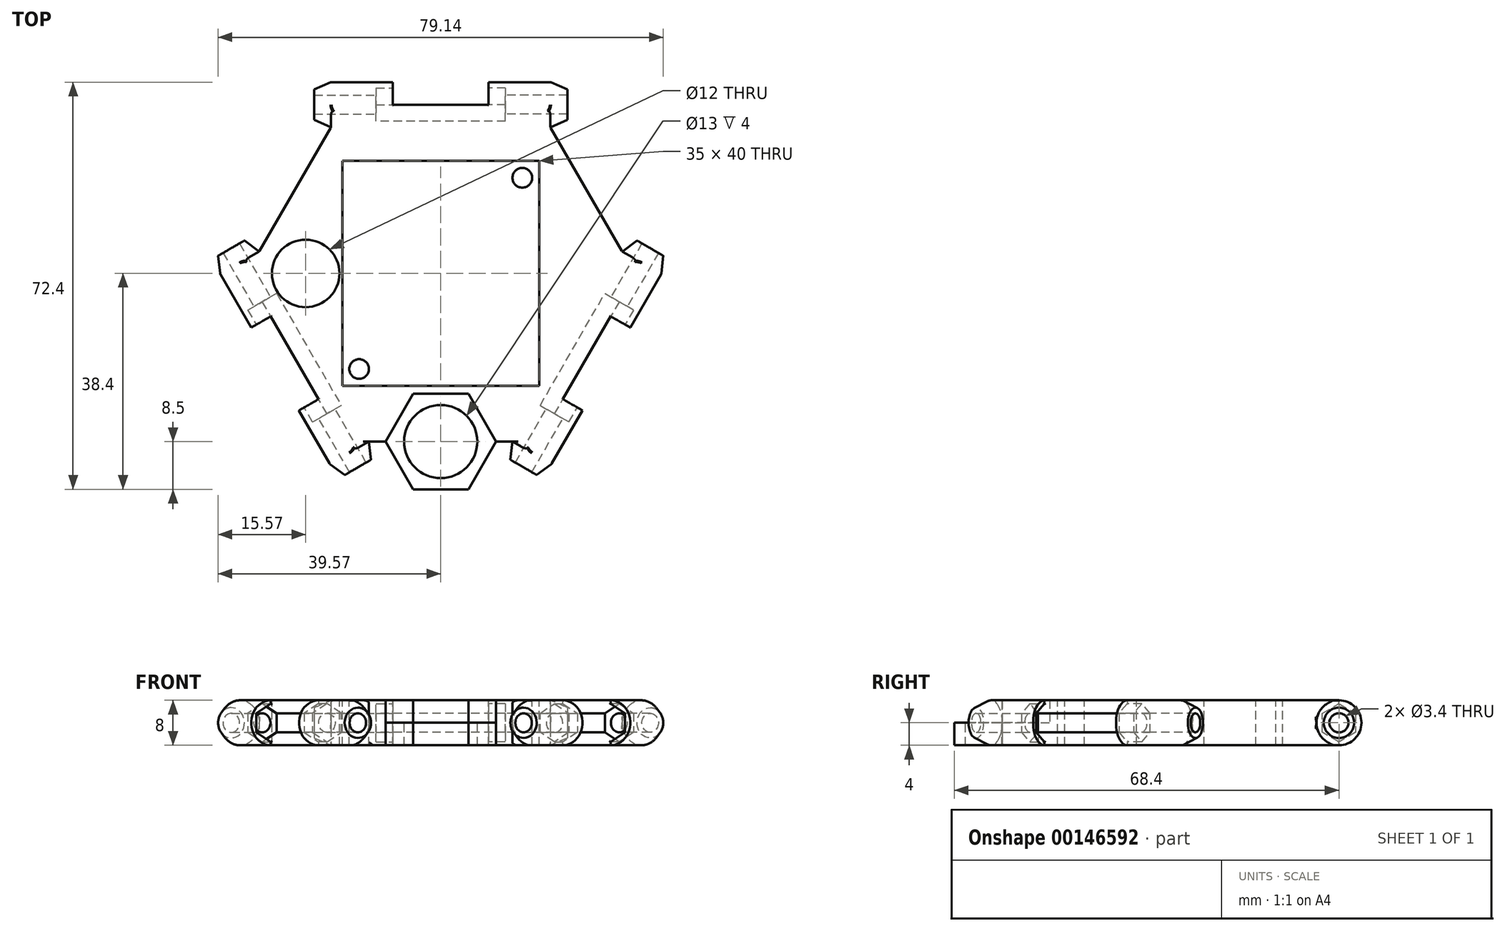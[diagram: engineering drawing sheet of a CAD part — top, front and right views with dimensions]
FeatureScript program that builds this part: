
annotation { "Feature Type Name" : "Feature", "Feature Type Description" : "" }
export const myFeature = defineFeature(function(context is Context, id is Id, definition is map)
    precondition{}
    {
        {
            var Q0;
            Q0=qCreatedBy(makeId("Top.planeOp"),FACE);
            var sketch = newSketch(context, id + "F0", { "sketchPlane" : qUnion([Q0])});
            skLineSegment(sketch, "E0.top", {"start": v(0, 34) * mm, "end": v(19.5, 34) * mm});
            skLineSegment(sketch, "E1", {"start": v(22.5, 31.7) * mm, "end": v(22.5, 32.7) * mm});
            skLineSegment(sketch, "E2", {"start": v(19.5, 34) * mm, "end": v(22.5, 32.7) * mm});
            skLineSegment(sketch, "E3", {"start": v(22.5, 31.7) * mm, "end": v(0, 31.7) * mm});
            skPoint(sketch, "E4.0.midPoint", {"position": v(0, 30) * mm});
            skLineSegment(sketch, "E5", {"start": v(19.5, 30) * mm, "end": v(36.82, 0) * mm, "construction": true});
            skLineSegment(sketch, "E6", {"start": v(0, 0) * mm, "end": v(27.62, 15.94) * mm, "construction": true});
            skLineSegment(sketch, "E7", {"start": v(0, 30) * mm, "end": v(22.5, 30) * mm, "construction": true});
            skLineSegment(sketch, "E8", {"start": v(0, 0) * mm, "end": v(0, 34) * mm});
            skLineSegment(sketch, "E9.MirrorCS", {"start": v(22.5, 28.3) * mm, "end": v(0, 28.3) * mm});
            skLineSegment(sketch, "E10.MirrorCS", {"start": v(0, 26) * mm, "end": v(19.5, 26) * mm});
            skLineSegment(sketch, "E11.MirrorCS", {"start": v(22.5, 28.3) * mm, "end": v(22.5, 27.3) * mm});
            skLineSegment(sketch, "E12.MirrorCS", {"start": v(19.5, 26) * mm, "end": v(22.5, 27.3) * mm});
            skLineSegment(sketch, "E13", {"start": v(19.5, 26) * mm, "end": v(32.2, 4) * mm, "construction": true});
            skLineSegment(sketch, "E14", {"start": v(0, 0) * mm, "end": v(25.88, 14.94) * mm});
            skLineSegment(sketch, "E15", {"start": v(19.5, 26) * mm, "end": v(25.88, 14.94) * mm});
            skSolve(sketch);
        }
        {
            var Q0;
            Q0=qCreatedBy(makeId("Right.planeOp"),FACE);
            var sketch = newSketch(context, id + "F1", { "sketchPlane" : qUnion([Q0])});
            skCircle(sketch, "E16.cCircle", {"center": v(30, 0) * mm, "radius": 2.95 * mm, "construction": true});
            skLineSegment(sketch, "E16.0", {"start": v(32.95, -1.7) * mm, "end": v(30, -3.4) * mm});
            skLineSegment(sketch, "E16.1", {"start": v(30, -3.4) * mm, "end": v(27.05, -1.7) * mm});
            skLineSegment(sketch, "E16.2", {"start": v(27.05, -1.7) * mm, "end": v(27.05, 1.7) * mm});
            skLineSegment(sketch, "E16.3", {"start": v(27.05, 1.7) * mm, "end": v(30, 3.4) * mm});
            skLineSegment(sketch, "E16.4", {"start": v(30, 3.4) * mm, "end": v(32.95, 1.7) * mm});
            skLineSegment(sketch, "E16.5", {"start": v(32.95, 1.7) * mm, "end": v(32.95, -1.7) * mm});
            skCircle(sketch, "E17", {"center": v(30, 0) * mm, "radius": 4 * mm});
            skLineSegment(sketch, "E18", {"start": v(26, 0) * mm, "end": v(26, -4) * mm});
            skLineSegment(sketch, "E19", {"start": v(26, -4) * mm, "end": v(30, -4) * mm});
            skLineSegment(sketch, "E20", {"start": v(30, 4) * mm, "end": v(30, -4) * mm, "construction": true});
            skLineSegment(sketch, "E21.MirrorCS", {"start": v(26, 4) * mm, "end": v(30, 4) * mm});
            skLineSegment(sketch, "E22.MirrorCS", {"start": v(26, 0) * mm, "end": v(26, 4) * mm});
            skLineSegment(sketch, "E23", {"start": v(0, 4) * mm, "end": v(0, -4) * mm, "construction": true});
            skLineSegment(sketch, "E24", {"start": v(30, 4) * mm, "end": v(30, 3.4) * mm});
            skLineSegment(sketch, "E25", {"start": v(30, -3.4) * mm, "end": v(30, -4) * mm});
            skSolve(sketch);
        }
        {
            var Q0;
            Q0=qCreatedBy(makeId("Top.planeOp"),FACE);
            var sketch = newSketch(context, id + "F2", { "sketchPlane" : qUnion([Q0])});
            skCircle(sketch, "E26.MirrorC", {"center": v(14.5, 17) * mm, "radius": 1.75 * mm});
            skLineSegment(sketch, "E27", {"start": v(0, 20) * mm, "end": v(17.5, 20) * mm, "construction": true});
            skLineSegment(sketch, "E28", {"start": v(17.5, 20) * mm, "end": v(17.5, 0) * mm, "construction": true});
            skLineSegment(sketch, "E29", {"start": v(17.5, 20) * mm, "end": v(0, 0) * mm, "construction": true});
            skCircle(sketch, "E30", {"center": v(10, 10) * mm, "radius": 4 * mm, "construction": true});
            skLineSegment(sketch, "E31", {"start": v(0, 10) * mm, "end": v(17.5, 10) * mm, "construction": true});
            skFitSpline(sketch, "E32", {"points": [v(12.53, 14.32) * mm, v(14.26, 12.62) * mm, v(15, 10) * mm], "startDerivative": vector(4.86, -2.41) * mm, "endDerivative": vector(0.41, -5.85) * mm});
            skLineSegment(sketch, "E33", {"start": v(15, 10) * mm, "end": v(15, 0) * mm});
            skLineSegment(sketch, "E34", {"start": v(12.53, 14.32) * mm, "end": v(2.46, 16.87) * mm});
            skLineSegment(sketch, "E35.MirrorCS", {"start": v(-12.53, 14.32) * mm, "end": v(-2.46, 16.87) * mm});
            skFitSpline(sketch, "E36.MirrorCS", {"points": [v(-12.53, 14.32) * mm, v(-14.26, 12.62) * mm, v(-15, 10) * mm], "startDerivative": vector(-4.86, -2.41) * mm, "endDerivative": vector(-0.41, -5.85) * mm});
            skLineSegment(sketch, "E37.MirrorCS", {"start": v(-15, 10) * mm, "end": v(-15, 0) * mm});
            skCircle(sketch, "E38.MirrorC", {"center": v(-14.5, 17) * mm, "radius": 1.75 * mm});
            skPoint(sketch, "E39.visualSharp", {"position": v(0, 17.5) * mm});
            skArc(sketch, "E39.filletArc", {"start": v(2.46, 16.87) * mm, "mid": v(0, 17.18) * mm, "end": v(-2.46, 16.87) * mm});
            skCircle(sketch, "E40.MirrorC", {"center": v(-14.5, -17) * mm, "radius": 1.75 * mm});
            skCircle(sketch, "E41.MirrorC", {"center": v(14.5, -17) * mm, "radius": 1.75 * mm});
            skLineSegment(sketch, "E42.MirrorCS", {"start": v(15, -10) * mm, "end": v(15, 0) * mm});
            skFitSpline(sketch, "E43.MirrorCS", {"points": [v(12.53, -14.32) * mm, v(14.26, -12.62) * mm, v(15, -10) * mm], "startDerivative": vector(4.86, 2.41) * mm, "endDerivative": vector(0.41, 5.85) * mm});
            skLineSegment(sketch, "E44.MirrorCS", {"start": v(12.53, -14.32) * mm, "end": v(2.46, -16.87) * mm});
            skArc(sketch, "E45.MirrorCS", {"start": v(2.46, -16.87) * mm, "mid": v(0, -17.18) * mm, "end": v(-2.46, -16.87) * mm});
            skLineSegment(sketch, "E46.MirrorCS", {"start": v(-12.53, -14.32) * mm, "end": v(-2.46, -16.87) * mm});
            skLineSegment(sketch, "E47.MirrorCS", {"start": v(-15, -10) * mm, "end": v(-15, 0) * mm});
            skFitSpline(sketch, "E48.MirrorCS", {"points": [v(-12.53, -14.32) * mm, v(-14.26, -12.62) * mm, v(-15, -10) * mm], "startDerivative": vector(-4.86, 2.41) * mm, "endDerivative": vector(-0.41, 5.85) * mm});
            skLineSegment(sketch, "E49.bottom", {"start": v(-17.5, 20) * mm, "end": v(17.5, 20) * mm});
            skLineSegment(sketch, "E49.top", {"start": v(-17.5, -20) * mm, "end": v(17.5, -20) * mm});
            skLineSegment(sketch, "E49.left", {"start": v(-17.5, 20) * mm, "end": v(-17.5, -20) * mm});
            skLineSegment(sketch, "E49.right", {"start": v(17.5, 20) * mm, "end": v(17.5, -20) * mm});
            skPoint(sketch, "E49.middle", {"position": v(0, 0) * mm});
            skCircle(sketch, "E50", {"center": v(-24, 0) * mm, "radius": 6 * mm});
            skCircle(sketch, "E51.MirrorC", {"center": v(24, 0) * mm, "radius": 6 * mm});
            skSolve(sketch);
        }
        {
            var Q0;
            {var subQ1=sQuery(id+"F0.wireOp",EDGE,"E0.top");Q0=makeQuery(id+"F0.imprint","IMPRINT",FACE,{"disambiguationData":[TD([[makeQuery(id+"F0.imprint","IMPRINT",EDGE,{"derivedFrom":subQ1}),-1.0]])]});}
            var Q1;
            Q1=sQuery(id+"F0.wireOp",EDGE,"E7");
            revolve(context, id + "F3", {"entities" : qUnion([Q0]), "axis" : qUnion([Q1]), "revolveType" : RevolveType.FULL});
        }
        {
            var Q0;
            {var subQ2=sQuery(id+"F1.wireOp",EDGE,"E21.MirrorCS");Q0=makeQuery(id+"F1.imprint","IMPRINT",FACE,{"disambiguationData":[TD([[makeQuery(id+"F1.imprint","IMPRINT",EDGE,{"derivedFrom":subQ2}),-1.0]])]});}
            var Q1;
            {var subQ0=sQuery(id+"F1.wireOp",EDGE,"E18");Q1=makeQuery(id+"F1.imprint","IMPRINT",FACE,{"disambiguationData":[TD([[makeQuery(id+"F1.imprint","IMPRINT",EDGE,{"derivedFrom":subQ0}),1.0]])]});}
            var Q2;
            {var subQ0=sQuery(id+"F1.wireOp",EDGE,"E19");var subQ1=sQuery(id+"F1.wireOp",EDGE,"E17");var subQ2=makeQuery(id+"F1.imprint","INTERSECT",VERTEX,{"derivedFrom":[subQ1,subQ0]});Q2=makeQuery(id+"F1.imprint","IMPRINT",FACE,{"disambiguationData":[TD([[makeQuery(id+"F1.imprint","IMPRINT",EDGE,{"disambiguationData":[TD([[subQ2,1.0]])],"derivedFrom":subQ1}),-1.0]])]});}
            var Q3;
            {var subQ0=sQuery(id+"F1.wireOp",EDGE,"E22.MirrorCS");Q3=makeQuery(id+"F1.imprint","IMPRINT",FACE,{"disambiguationData":[TD([[makeQuery(id+"F1.imprint","IMPRINT",EDGE,{"derivedFrom":subQ0}),-1.0]])]});}
            extrude(context, id + "F4", {"entities" : qUnion([Q0, Q1, Q2, Q3]), "operationType" : NewBodyOperationType.ADD, "depth" : 19.5 * mm});
        }
        {
            var Q0;
            {var subQ2=sQuery(id+"F0.wireOp",EDGE,"E10.MirrorCS");Q0=makeQuery(id+"F0.imprint","IMPRINT",FACE,{"disambiguationData":[TD([[makeQuery(id+"F0.imprint","IMPRINT",EDGE,{"derivedFrom":subQ2}),-1.0]])]});}
            extrude(context, id + "F5", {"entities" : qUnion([Q0]), "operationType" : NewBodyOperationType.ADD, "endBound" : BoundingType.SYMMETRIC, "depth" : 8 * mm});
        }
        {
            var Q0;
            Q0=makeQuery(id+"F1.imprint","IMPRINT",FACE,{"disambiguationData":[TD([[makeQuery(id+"F1.imprint","IMPRINT",EDGE,{"derivedFrom":sQuery(id+"F1.wireOp",EDGE,"E16.0")}),-1.0]])]});
            extrude(context, id + "F6", {"entities" : qUnion([Q0]), "operationType" : NewBodyOperationType.REMOVE, "depth" : (45 / 2 - 11) * mm});
        }
        {
            var Q0;
            Q0=makeQuery(id+"F1.imprint","IMPRINT",FACE,{"disambiguationData":[TD([[makeQuery(id+"F1.imprint","IMPRINT",EDGE,{"derivedFrom":sQuery(id+"F1.wireOp",EDGE,"E16.0")}),1.0]])]});
            extrude(context, id + "F7", {"entities" : qUnion([Q0]), "operationType" : NewBodyOperationType.REMOVE, "depth" : (45 / 2 - 14) * mm});
        }
        {
            var Q0;
            Q0=makeQuery(id+"F3.opRevolve","SWEPT_BODY",BODY,{"disambiguationData":[OSD([sQuery(id+"F0.wireOp",EDGE,"E0.top"),sQuery(id+"F0.wireOp",EDGE,"E0.left"),sQuery(id+"F0.wireOp",EDGE,"E1"),sQuery(id+"F0.wireOp",EDGE,"E2"),sQuery(id+"F0.wireOp",EDGE,"E3")])]});
            var Q1;
            Q1=qCreatedBy(makeId("Right.planeOp"),FACE);
            mirror(context, id + "F8", {"operationType" : NewBodyOperationType.ADD, "entities" : qUnion([Q0]), "mirrorPlane" : qUnion([Q1])});
        }
        {
            var Q0;
            Q0=makeQuery(id+"F3.opRevolve","SWEPT_BODY",BODY,{"disambiguationData":[OSD([sQuery(id+"F0.wireOp",EDGE,"E0.top"),sQuery(id+"F0.wireOp",EDGE,"E0.left"),sQuery(id+"F0.wireOp",EDGE,"E1"),sQuery(id+"F0.wireOp",EDGE,"E2"),sQuery(id+"F0.wireOp",EDGE,"E3")])]});
            var Q1;
            Q1=makeQuery(id+"F3.opRevolve","SWEPT_BODY",BODY,{"disambiguationData":[OSD([sQuery(id+"F0.wireOp",EDGE,"E8"),sQuery(id+"F0.wireOp",EDGE,"E9.MirrorCS"),sQuery(id+"F0.wireOp",EDGE,"E10.MirrorCS"),sQuery(id+"F0.wireOp",EDGE,"E11.MirrorCS"),sQuery(id+"F0.wireOp",EDGE,"E12.MirrorCS")])]});
            var Q2;
            Q2=sQuery(id+"F1.wireOp",EDGE,"E23");
            circularPattern(context, id + "F9", {"operationType" : NewBodyOperationType.ADD, "entities" : qUnion([Q0, Q1]), "axis" : qUnion([Q2]), "angle" : 120 * degree, "instanceCount" : 3});
        }
        {
            var Q0;
            Q0=makeQuery(id+"F2.imprint","IMPRINT",FACE,{"disambiguationData":[TD([[makeQuery(id+"F2.imprint","IMPRINT",EDGE,{"derivedFrom":sQuery(id+"F2.wireOp",EDGE,"E32")}),-1.0]])]});
            var Q1;
            Q1=makeQuery(id+"F2.imprint","IMPRINT",FACE,{"disambiguationData":[TD([[makeQuery(id+"F2.imprint","IMPRINT",EDGE,{"derivedFrom":sQuery(id+"F2.wireOp",EDGE,"E38.MirrorC")}),1.0]])]});
            var Q2;
            Q2=makeQuery(id+"F2.imprint","IMPRINT",FACE,{"disambiguationData":[TD([[makeQuery(id+"F2.imprint","IMPRINT",EDGE,{"derivedFrom":sQuery(id+"F2.wireOp",EDGE,"E26.MirrorC")}),-1.0]])]});
            var Q3;
            Q3=makeQuery(id+"F2.imprint","IMPRINT",FACE,{"disambiguationData":[TD([[makeQuery(id+"F2.imprint","IMPRINT",EDGE,{"derivedFrom":sQuery(id+"F2.wireOp",EDGE,"E41.MirrorC")}),1.0]])]});
            var Q4;
            Q4=makeQuery(id+"F2.imprint","IMPRINT",FACE,{"disambiguationData":[TD([[makeQuery(id+"F2.imprint","IMPRINT",EDGE,{"derivedFrom":sQuery(id+"F2.wireOp",EDGE,"E40.MirrorC")}),-1.0]])]});
            var Q5;
            Q5=makeQuery(id+"F2.imprint","IMPRINT",FACE,{"disambiguationData":[TD([[makeQuery(id+"F2.imprint","IMPRINT",EDGE,{"derivedFrom":sQuery(id+"F2.wireOp",EDGE,"E50")}),1.0]])]});
            var Q6;
            Q6=makeQuery(id+"F2.imprint","IMPRINT",FACE,{"disambiguationData":[TD([[makeQuery(id+"F2.imprint","IMPRINT",EDGE,{"derivedFrom":sQuery(id+"F2.wireOp",EDGE,"E51.MirrorC")}),-1.0]])]});
            var Q7;
            {var subQ0=sQuery(id+"F2.wireOp",EDGE,"E50");var subQ1=sQuery(id+"F2.wireOp",EDGE,"JJTMQ2RY-KDWr-5WRS-YdwC-lt0RPVDN6D57.right");var subQ2=makeQuery(id+"F2.imprint","INTERSECT",VERTEX,{"disambiguationData":[OD(0.0)],"derivedFrom":[subQ1,subQ0]});Q7=makeQuery(id+"F2.imprint","IMPRINT",FACE,{"disambiguationData":[TD([[makeQuery(id+"F2.imprint","IMPRINT",EDGE,{"disambiguationData":[TD([[subQ2,-1.0]])],"derivedFrom":subQ1}),1.0]])]});}
            var Q8;
            {var subQ0=sQuery(id+"F2.wireOp",EDGE,"E51.MirrorC");var subQ1=sQuery(id+"F2.wireOp",EDGE,"JJTMQ2RY-KDWr-5WRS-YdwC-lt0RPVDN6D57.left");var subQ2=makeQuery(id+"F2.imprint","INTERSECT",VERTEX,{"disambiguationData":[OD(0.0)],"derivedFrom":[subQ1,subQ0]});Q8=makeQuery(id+"F2.imprint","IMPRINT",FACE,{"disambiguationData":[TD([[makeQuery(id+"F2.imprint","IMPRINT",EDGE,{"disambiguationData":[TD([[subQ2,-1.0]])],"derivedFrom":subQ1}),-1.0]])]});}
            extrude(context, id + "F10", {"entities" : qUnion([Q0, Q1, Q2, Q3, Q4, Q5, Q6, Q7, Q8]), "operationType" : NewBodyOperationType.REMOVE, "endBound" : BoundingType.SYMMETRIC, "oppositeDirection" : true, "depth" : 8 * mm});
        }
        {
            var Q0;
            Q0=qCreatedBy(makeId("Top.planeOp"),FACE);
            var sketch = newSketch(context, id + "F11", { "sketchPlane" : qUnion([Q0])});
            skCircle(sketch, "E52.cCircle", {"center": v(0, -29.9) * mm, "radius": 8.5 * mm, "construction": true});
            skLineSegment(sketch, "E52.0", {"start": v(-4.9, -21.4) * mm, "end": v(4.9, -21.4) * mm});
            skLineSegment(sketch, "E52.1", {"start": v(4.9, -21.4) * mm, "end": v(9.81, -29.9) * mm});
            skLineSegment(sketch, "E52.2", {"start": v(9.81, -29.9) * mm, "end": v(4.9, -38.4) * mm});
            skLineSegment(sketch, "E52.3", {"start": v(4.9, -38.4) * mm, "end": v(-4.9, -38.4) * mm});
            skLineSegment(sketch, "E52.4", {"start": v(-4.9, -38.4) * mm, "end": v(-9.81, -29.9) * mm});
            skLineSegment(sketch, "E52.5", {"start": v(-9.81, -29.9) * mm, "end": v(-4.9, -21.4) * mm});
            skPoint(sketch, "E52.0.midPoint", {"position": v(0, -21.4) * mm});
            skCircle(sketch, "E53", {"center": v(0, -29.9) * mm, "radius": 6.5 * mm});
            skCircle(sketch, "E54", {"center": v(0, -29.9) * mm, "radius": 10 * mm});
            skSolve(sketch);
        }
        {
            var Q0;
            Q0=makeQuery(id+"F11.imprint","IMPRINT",FACE,{"disambiguationData":[TD([[makeQuery(id+"F11.imprint","IMPRINT",EDGE,{"derivedFrom":sQuery(id+"F11.wireOp",EDGE,"E53")}),1.0]])]});
            var Q1;
            Q1=makeQuery(id+"F11.imprint","IMPRINT",FACE,{"disambiguationData":[TD([[makeQuery(id+"F11.imprint","IMPRINT",EDGE,{"derivedFrom":sQuery(id+"F11.wireOp",EDGE,"E52.0")}),-1.0]])]});
            extrude(context, id + "F12", {"entities" : qUnion([Q0, Q1]), "operationType" : NewBodyOperationType.REMOVE, "endBound" : BoundingType.SYMMETRIC, "depth" : 40 * mm});
        }
        {
            var Q0;
            Q0=makeQuery(id+"F11.imprint","IMPRINT",FACE,{"disambiguationData":[TD([[makeQuery(id+"F11.imprint","IMPRINT",EDGE,{"derivedFrom":sQuery(id+"F11.wireOp",EDGE,"E52.0")}),-1.0]])]});
            extrude(context, id + "F13", {"entities" : qUnion([Q0]), "operationType" : NewBodyOperationType.ADD, "oppositeDirection" : true, "depth" : 4 * mm});
        }
        {
            var Q0;
            Q0=makeQuery(id+"FdFZlNH1jCsqDf1_2.opExtrude","CAP_EDGE",EDGE,{"disambiguationData":[OSD([sQuery(id+"F11.wireOp",EDGE,"E54")])],"isStart":false});
            var Q1;
            Q1=makeQuery(id+"F9.opPattern","COPY",EDGE,{"derivedFrom":makeQuery(id+"F4.opExtrude","CAP_EDGE",EDGE,{"disambiguationData":[OSD([sQuery(id+"F1.wireOp",EDGE,"E21.MirrorCS")])],"isStart":false}),"instanceName":"1"});
            var Q2;
            {var subQ1=sQuery(id+"F0.wireOp",EDGE,"E15");var subQ8=makeQuery(id+"F5.opExtrude","CAP_EDGE",EDGE,{"disambiguationData":[OSD([subQ1])],"isStart":false});Q2=makeQuery(id+"F12.boolean.opBoolean","SPLIT",EDGE,{"disambiguationData":[TD([makeQuery(id+"F12.opExtrude","SWEPT_FACE",FACE,{"disambiguationData":[OSD([sQuery(id+"F11.wireOp",EDGE,"E52.2")])]})])],"derivedFrom":makeQuery(id+"F9.boolean.opBoolean","MERGE",EDGE,{"derivedFrom":[makeQuery(id+"F9.opPattern","COPY",EDGE,{"derivedFrom":subQ8,"instanceName":"1"}),makeQuery(id+"F9.opPattern","COPY",EDGE,{"derivedFrom":makeQuery(id+"F8.opPattern","COPY",EDGE,{"derivedFrom":subQ8,"instanceName":"1"}),"instanceName":"2"})]})});}
            var Q3;
            Q3=makeQuery(id+"F9.opPattern","COPY",EDGE,{"derivedFrom":makeQuery(id+"F8.opPattern","COPY",EDGE,{"derivedFrom":makeQuery(id+"F5.boolean.opBoolean","MERGE",EDGE,{"derivedFrom":[makeQuery(id+"F4.opExtrude","CAP_EDGE",EDGE,{"disambiguationData":[OSD([sQuery(id+"F1.wireOp",EDGE,"E22.MirrorCS")])],"isStart":false}),makeQuery(id+"F5.opExtrude","SWEPT_EDGE",EDGE,{"disambiguationData":[OSD([sQuery(id+"F0.wireOp",EDGE,"E10.MirrorCS"),sQuery(id+"F0.wireOp",EDGE,"E12.MirrorCS"),sQuery(id+"F0.wireOp",EDGE,"E15")])]})]}),"instanceName":"1"}),"instanceName":"1"});
            var Q4;
            {var subQ0=makeQuery(id+"F5.opExtrude","CAP_EDGE",EDGE,{"disambiguationData":[OSD([sQuery(id+"F0.wireOp",EDGE,"E15")])],"isStart":false});Q4=makeQuery(id+"F9.boolean.opBoolean","MERGE",EDGE,{"derivedFrom":[subQ0,makeQuery(id+"F9.opPattern","COPY",EDGE,{"derivedFrom":makeQuery(id+"F8.opPattern","COPY",EDGE,{"derivedFrom":subQ0,"instanceName":"1"}),"instanceName":"1"})]});}
            var Q5;
            Q5=makeQuery(id+"F4.opExtrude","CAP_EDGE",EDGE,{"disambiguationData":[OSD([sQuery(id+"F1.wireOp",EDGE,"E21.MirrorCS")])],"isStart":false});
            var Q6;
            {var subQ0=sQuery(id+"F1.wireOp",EDGE,"E24");var subQ1=sQuery(id+"F1.wireOp",EDGE,"E21.MirrorCS");var subQ2=sQuery(id+"F1.wireOp",EDGE,"E17");var subQ3=makeQuery(id+"F7.boolean.opBoolean","MERGE",EDGE,{"derivedFrom":[makeQuery(id+"F4.opExtrude","SWEPT_EDGE",EDGE,{"disambiguationData":[OSD([subQ2,subQ1,subQ0])]}),makeQuery(id+"F7.opExtrude","SWEPT_EDGE",EDGE,{"disambiguationData":[OSD([subQ2,subQ1,subQ0])]})]});Q6=makeQuery(id+"F9.opPattern","COPY",EDGE,{"derivedFrom":makeQuery(id+"F8.boolean.opBoolean","MERGE",EDGE,{"derivedFrom":[subQ3,makeQuery(id+"F8.opPattern","COPY",EDGE,{"derivedFrom":subQ3,"instanceName":"1"})]}),"instanceName":"1"});}
            var Q7;
            {var subQ0=sQuery(id+"F1.wireOp",EDGE,"E24");var subQ1=sQuery(id+"F1.wireOp",EDGE,"E16.4");var subQ2=sQuery(id+"F1.wireOp",EDGE,"E16.3");var subQ3=makeQuery(id+"F7.boolean.opBoolean","MERGE",EDGE,{"derivedFrom":[makeQuery(id+"F6.boolean.opBoolean","COPY",EDGE,{"derivedFrom":makeQuery(id+"F6.opExtrude","SWEPT_EDGE",EDGE,{"disambiguationData":[OSD([subQ2,subQ1,subQ0])]})}),makeQuery(id+"F7.opExtrude","SWEPT_EDGE",EDGE,{"disambiguationData":[OSD([subQ2,subQ1,subQ0])]})]});Q7=makeQuery(id+"F9.opPattern","COPY",EDGE,{"derivedFrom":makeQuery(id+"F8.boolean.opBoolean","MERGE",EDGE,{"derivedFrom":[subQ3,makeQuery(id+"F8.opPattern","COPY",EDGE,{"derivedFrom":subQ3,"instanceName":"1"})]}),"instanceName":"1"});}
            var Q8;
            Q8=makeQuery(id+"F9.opPattern","COPY",EDGE,{"derivedFrom":makeQuery(id+"F4.boolean.opBoolean","SPLIT",EDGE,{"derivedFrom":makeQuery(id+"F3.opRevolve","SWEPT_EDGE",EDGE,{"disambiguationData":[OSD([sQuery(id+"F0.wireOp",EDGE,"E0.top"),sQuery(id+"F0.wireOp",EDGE,"E2")])]})}),"instanceName":"1"});
            var Q9;
            Q9=makeQuery(id+"F9.opPattern","COPY",EDGE,{"derivedFrom":makeQuery(id+"F8.opPattern","COPY",EDGE,{"derivedFrom":makeQuery(id+"F4.boolean.opBoolean","SPLIT",EDGE,{"derivedFrom":makeQuery(id+"F3.opRevolve","SWEPT_EDGE",EDGE,{"disambiguationData":[OSD([sQuery(id+"F0.wireOp",EDGE,"E0.top"),sQuery(id+"F0.wireOp",EDGE,"E2")])]})}),"instanceName":"1"}),"instanceName":"1"});
            var Q10;
            {var subQ0=sQuery(id+"F1.wireOp",EDGE,"E25");var subQ1=sQuery(id+"F1.wireOp",EDGE,"E16.1");var subQ2=sQuery(id+"F1.wireOp",EDGE,"E16.0");var subQ3=makeQuery(id+"F7.boolean.opBoolean","MERGE",EDGE,{"derivedFrom":[makeQuery(id+"F6.boolean.opBoolean","COPY",EDGE,{"derivedFrom":makeQuery(id+"F6.opExtrude","SWEPT_EDGE",EDGE,{"disambiguationData":[OSD([subQ2,subQ1,subQ0])]})}),makeQuery(id+"F7.opExtrude","SWEPT_EDGE",EDGE,{"disambiguationData":[OSD([subQ2,subQ1,subQ0])]})]});Q10=makeQuery(id+"F9.opPattern","COPY",EDGE,{"derivedFrom":makeQuery(id+"F8.boolean.opBoolean","MERGE",EDGE,{"derivedFrom":[subQ3,makeQuery(id+"F8.opPattern","COPY",EDGE,{"derivedFrom":subQ3,"instanceName":"1"})]}),"instanceName":"1"});}
            var Q11;
            {var subQ0=sQuery(id+"F1.wireOp",EDGE,"E25");var subQ1=sQuery(id+"F1.wireOp",EDGE,"E19");var subQ2=sQuery(id+"F1.wireOp",EDGE,"E17");var subQ3=makeQuery(id+"F7.boolean.opBoolean","MERGE",EDGE,{"derivedFrom":[makeQuery(id+"F4.opExtrude","SWEPT_EDGE",EDGE,{"disambiguationData":[OSD([subQ2,subQ1,subQ0])]}),makeQuery(id+"F7.opExtrude","SWEPT_EDGE",EDGE,{"disambiguationData":[OSD([subQ2,subQ1,subQ0])]})]});Q11=makeQuery(id+"F9.opPattern","COPY",EDGE,{"derivedFrom":makeQuery(id+"F8.boolean.opBoolean","MERGE",EDGE,{"derivedFrom":[subQ3,makeQuery(id+"F8.opPattern","COPY",EDGE,{"derivedFrom":subQ3,"instanceName":"1"})]}),"instanceName":"1"});}
            var Q12;
            {var subQ0=sQuery(id+"F0.wireOp",EDGE,"E15");var subQ8=makeQuery(id+"F5.opExtrude","CAP_EDGE",EDGE,{"disambiguationData":[OSD([subQ0])],"isStart":false});Q12=makeQuery(id+"F12.boolean.opBoolean","SPLIT",EDGE,{"disambiguationData":[TD([makeQuery(id+"F12.opExtrude","SWEPT_FACE",FACE,{"disambiguationData":[OSD([sQuery(id+"F11.wireOp",EDGE,"E52.4")])]})])],"derivedFrom":makeQuery(id+"F9.boolean.opBoolean","MERGE",EDGE,{"derivedFrom":[makeQuery(id+"F9.opPattern","COPY",EDGE,{"derivedFrom":subQ8,"instanceName":"1"}),makeQuery(id+"F9.opPattern","COPY",EDGE,{"derivedFrom":makeQuery(id+"F8.opPattern","COPY",EDGE,{"derivedFrom":subQ8,"instanceName":"1"}),"instanceName":"2"})]})});}
            var Q13;
            Q13=makeQuery(id+"F9.opPattern","COPY",EDGE,{"derivedFrom":makeQuery(id+"F8.opPattern","COPY",EDGE,{"derivedFrom":makeQuery(id+"F4.opExtrude","CAP_EDGE",EDGE,{"disambiguationData":[OSD([sQuery(id+"F1.wireOp",EDGE,"E21.MirrorCS")])],"isStart":false}),"instanceName":"1"}),"instanceName":"2"});
            var Q14;
            Q14=makeQuery(id+"F9.opPattern","COPY",EDGE,{"derivedFrom":makeQuery(id+"F4.opExtrude","CAP_EDGE",EDGE,{"disambiguationData":[OSD([sQuery(id+"F1.wireOp",EDGE,"E21.MirrorCS")])],"isStart":false}),"instanceName":"2"});
            var Q15;
            {var subQ0=makeQuery(id+"F5.opExtrude","CAP_EDGE",EDGE,{"disambiguationData":[OSD([sQuery(id+"F0.wireOp",EDGE,"E15")])],"isStart":false});Q15=makeQuery(id+"F9.boolean.opBoolean","MERGE",EDGE,{"derivedFrom":[makeQuery(id+"F8.opPattern","COPY",EDGE,{"derivedFrom":subQ0,"instanceName":"1"}),makeQuery(id+"F9.opPattern","COPY",EDGE,{"derivedFrom":subQ0,"instanceName":"2"})]});}
            var Q16;
            {var subQ0=makeQuery(id+"F5.opExtrude","CAP_EDGE",EDGE,{"disambiguationData":[OSD([sQuery(id+"F0.wireOp",EDGE,"E15")])],"isStart":true});Q16=makeQuery(id+"F9.boolean.opBoolean","MERGE",EDGE,{"derivedFrom":[subQ0,makeQuery(id+"F9.opPattern","COPY",EDGE,{"derivedFrom":makeQuery(id+"F8.opPattern","COPY",EDGE,{"derivedFrom":subQ0,"instanceName":"1"}),"instanceName":"1"})]});}
            var Q17;
            Q17=makeQuery(id+"F9.opPattern","COPY",EDGE,{"derivedFrom":makeQuery(id+"F8.opPattern","COPY",EDGE,{"derivedFrom":makeQuery(id+"F5.boolean.opBoolean","MERGE",EDGE,{"derivedFrom":[makeQuery(id+"F4.opExtrude","CAP_EDGE",EDGE,{"disambiguationData":[OSD([sQuery(id+"F1.wireOp",EDGE,"E18")])],"isStart":false}),makeQuery(id+"F5.opExtrude","SWEPT_EDGE",EDGE,{"disambiguationData":[OSD([sQuery(id+"F0.wireOp",EDGE,"E10.MirrorCS"),sQuery(id+"F0.wireOp",EDGE,"E12.MirrorCS"),sQuery(id+"F0.wireOp",EDGE,"E15")])]})]}),"instanceName":"1"}),"instanceName":"1"});
            var Q18;
            Q18=makeQuery(id+"F5.boolean.opBoolean","MERGE",EDGE,{"derivedFrom":[makeQuery(id+"F4.opExtrude","CAP_EDGE",EDGE,{"disambiguationData":[OSD([sQuery(id+"F1.wireOp",EDGE,"E22.MirrorCS")])],"isStart":false}),makeQuery(id+"F5.opExtrude","SWEPT_EDGE",EDGE,{"disambiguationData":[OSD([sQuery(id+"F0.wireOp",EDGE,"E10.MirrorCS"),sQuery(id+"F0.wireOp",EDGE,"E12.MirrorCS"),sQuery(id+"F0.wireOp",EDGE,"E15")])]})]});
            var Q19;
            Q19=makeQuery(id+"F5.boolean.opBoolean","MERGE",EDGE,{"derivedFrom":[makeQuery(id+"F4.opExtrude","CAP_EDGE",EDGE,{"disambiguationData":[OSD([sQuery(id+"F1.wireOp",EDGE,"E18")])],"isStart":false}),makeQuery(id+"F5.opExtrude","SWEPT_EDGE",EDGE,{"disambiguationData":[OSD([sQuery(id+"F0.wireOp",EDGE,"E10.MirrorCS"),sQuery(id+"F0.wireOp",EDGE,"E12.MirrorCS"),sQuery(id+"F0.wireOp",EDGE,"E15")])]})]});
            var Q20;
            {var subQ1=sQuery(id+"F0.wireOp",EDGE,"E15");var subQ8=makeQuery(id+"F5.opExtrude","CAP_EDGE",EDGE,{"disambiguationData":[OSD([subQ1])],"isStart":true});Q20=makeQuery(id+"F12.boolean.opBoolean","SPLIT",EDGE,{"disambiguationData":[TD([makeQuery(id+"F12.opExtrude","SWEPT_FACE",FACE,{"disambiguationData":[OSD([sQuery(id+"F11.wireOp",EDGE,"E52.2")])]})])],"derivedFrom":makeQuery(id+"F9.boolean.opBoolean","MERGE",EDGE,{"derivedFrom":[makeQuery(id+"F9.opPattern","COPY",EDGE,{"derivedFrom":subQ8,"instanceName":"1"}),makeQuery(id+"F9.opPattern","COPY",EDGE,{"derivedFrom":makeQuery(id+"F8.opPattern","COPY",EDGE,{"derivedFrom":subQ8,"instanceName":"1"}),"instanceName":"2"})]})});}
            var Q21;
            Q21=makeQuery(id+"F9.opPattern","COPY",EDGE,{"derivedFrom":makeQuery(id+"F4.opExtrude","CAP_EDGE",EDGE,{"disambiguationData":[OSD([sQuery(id+"F1.wireOp",EDGE,"E19")])],"isStart":false}),"instanceName":"1"});
            var Q22;
            {var subQ0=sQuery(id+"F0.wireOp",EDGE,"E15");var subQ8=makeQuery(id+"F5.opExtrude","CAP_EDGE",EDGE,{"disambiguationData":[OSD([subQ0])],"isStart":true});Q22=makeQuery(id+"F12.boolean.opBoolean","SPLIT",EDGE,{"disambiguationData":[TD([makeQuery(id+"F12.opExtrude","SWEPT_FACE",FACE,{"disambiguationData":[OSD([sQuery(id+"F11.wireOp",EDGE,"E52.4")])]})])],"derivedFrom":makeQuery(id+"F9.boolean.opBoolean","MERGE",EDGE,{"derivedFrom":[makeQuery(id+"F9.opPattern","COPY",EDGE,{"derivedFrom":subQ8,"instanceName":"1"}),makeQuery(id+"F9.opPattern","COPY",EDGE,{"derivedFrom":makeQuery(id+"F8.opPattern","COPY",EDGE,{"derivedFrom":subQ8,"instanceName":"1"}),"instanceName":"2"})]})});}
            var Q23;
            Q23=makeQuery(id+"F9.opPattern","COPY",EDGE,{"derivedFrom":makeQuery(id+"F8.opPattern","COPY",EDGE,{"derivedFrom":makeQuery(id+"F4.opExtrude","CAP_EDGE",EDGE,{"disambiguationData":[OSD([sQuery(id+"F1.wireOp",EDGE,"E19")])],"isStart":false}),"instanceName":"1"}),"instanceName":"2"});
            var Q24;
            Q24=makeQuery(id+"F9.opPattern","COPY",EDGE,{"derivedFrom":makeQuery(id+"F8.opPattern","COPY",EDGE,{"derivedFrom":makeQuery(id+"F5.boolean.opBoolean","MERGE",EDGE,{"derivedFrom":[makeQuery(id+"F4.opExtrude","CAP_EDGE",EDGE,{"disambiguationData":[OSD([sQuery(id+"F1.wireOp",EDGE,"E18")])],"isStart":false}),makeQuery(id+"F5.opExtrude","SWEPT_EDGE",EDGE,{"disambiguationData":[OSD([sQuery(id+"F0.wireOp",EDGE,"E10.MirrorCS"),sQuery(id+"F0.wireOp",EDGE,"E12.MirrorCS"),sQuery(id+"F0.wireOp",EDGE,"E15")])]})]}),"instanceName":"1"}),"instanceName":"2"});
            var Q25;
            {var subQ0=sQuery(id+"F1.wireOp",EDGE,"E24");var subQ1=sQuery(id+"F1.wireOp",EDGE,"E21.MirrorCS");var subQ2=sQuery(id+"F1.wireOp",EDGE,"E17");var subQ3=makeQuery(id+"F7.boolean.opBoolean","MERGE",EDGE,{"derivedFrom":[makeQuery(id+"F4.opExtrude","SWEPT_EDGE",EDGE,{"disambiguationData":[OSD([subQ2,subQ1,subQ0])]}),makeQuery(id+"F7.opExtrude","SWEPT_EDGE",EDGE,{"disambiguationData":[OSD([subQ2,subQ1,subQ0])]})]});Q25=makeQuery(id+"F9.opPattern","COPY",EDGE,{"derivedFrom":makeQuery(id+"F8.boolean.opBoolean","MERGE",EDGE,{"derivedFrom":[subQ3,makeQuery(id+"F8.opPattern","COPY",EDGE,{"derivedFrom":subQ3,"instanceName":"1"})]}),"instanceName":"2"});}
            var Q26;
            {var subQ0=sQuery(id+"F1.wireOp",EDGE,"E24");var subQ1=sQuery(id+"F1.wireOp",EDGE,"E16.4");var subQ2=sQuery(id+"F1.wireOp",EDGE,"E16.3");var subQ3=makeQuery(id+"F7.boolean.opBoolean","MERGE",EDGE,{"derivedFrom":[makeQuery(id+"F6.boolean.opBoolean","COPY",EDGE,{"derivedFrom":makeQuery(id+"F6.opExtrude","SWEPT_EDGE",EDGE,{"disambiguationData":[OSD([subQ2,subQ1,subQ0])]})}),makeQuery(id+"F7.opExtrude","SWEPT_EDGE",EDGE,{"disambiguationData":[OSD([subQ2,subQ1,subQ0])]})]});Q26=makeQuery(id+"F9.opPattern","COPY",EDGE,{"derivedFrom":makeQuery(id+"F8.boolean.opBoolean","MERGE",EDGE,{"derivedFrom":[subQ3,makeQuery(id+"F8.opPattern","COPY",EDGE,{"derivedFrom":subQ3,"instanceName":"1"})]}),"instanceName":"2"});}
            var Q27;
            {var subQ0=sQuery(id+"F1.wireOp",EDGE,"E25");var subQ1=sQuery(id+"F1.wireOp",EDGE,"E16.1");var subQ2=sQuery(id+"F1.wireOp",EDGE,"E16.0");var subQ3=makeQuery(id+"F7.boolean.opBoolean","MERGE",EDGE,{"derivedFrom":[makeQuery(id+"F6.boolean.opBoolean","COPY",EDGE,{"derivedFrom":makeQuery(id+"F6.opExtrude","SWEPT_EDGE",EDGE,{"disambiguationData":[OSD([subQ2,subQ1,subQ0])]})}),makeQuery(id+"F7.opExtrude","SWEPT_EDGE",EDGE,{"disambiguationData":[OSD([subQ2,subQ1,subQ0])]})]});Q27=makeQuery(id+"F9.opPattern","COPY",EDGE,{"derivedFrom":makeQuery(id+"F8.boolean.opBoolean","MERGE",EDGE,{"derivedFrom":[subQ3,makeQuery(id+"F8.opPattern","COPY",EDGE,{"derivedFrom":subQ3,"instanceName":"1"})]}),"instanceName":"2"});}
            var Q28;
            {var subQ0=sQuery(id+"F1.wireOp",EDGE,"E25");var subQ1=sQuery(id+"F1.wireOp",EDGE,"E19");var subQ2=sQuery(id+"F1.wireOp",EDGE,"E17");var subQ3=makeQuery(id+"F7.boolean.opBoolean","MERGE",EDGE,{"derivedFrom":[makeQuery(id+"F4.opExtrude","SWEPT_EDGE",EDGE,{"disambiguationData":[OSD([subQ2,subQ1,subQ0])]}),makeQuery(id+"F7.opExtrude","SWEPT_EDGE",EDGE,{"disambiguationData":[OSD([subQ2,subQ1,subQ0])]})]});Q28=makeQuery(id+"F9.opPattern","COPY",EDGE,{"derivedFrom":makeQuery(id+"F8.boolean.opBoolean","MERGE",EDGE,{"derivedFrom":[subQ3,makeQuery(id+"F8.opPattern","COPY",EDGE,{"derivedFrom":subQ3,"instanceName":"1"})]}),"instanceName":"2"});}
            var Q29;
            Q29=makeQuery(id+"F9.opPattern","COPY",EDGE,{"derivedFrom":makeQuery(id+"F5.boolean.opBoolean","MERGE",EDGE,{"derivedFrom":[makeQuery(id+"F4.opExtrude","CAP_EDGE",EDGE,{"disambiguationData":[OSD([sQuery(id+"F1.wireOp",EDGE,"E18")])],"isStart":false}),makeQuery(id+"F5.opExtrude","SWEPT_EDGE",EDGE,{"disambiguationData":[OSD([sQuery(id+"F0.wireOp",EDGE,"E10.MirrorCS"),sQuery(id+"F0.wireOp",EDGE,"E12.MirrorCS"),sQuery(id+"F0.wireOp",EDGE,"E15")])]})]}),"instanceName":"2"});
            var Q30;
            Q30=makeQuery(id+"F9.opPattern","COPY",EDGE,{"derivedFrom":makeQuery(id+"F5.boolean.opBoolean","MERGE",EDGE,{"derivedFrom":[makeQuery(id+"F4.opExtrude","CAP_EDGE",EDGE,{"disambiguationData":[OSD([sQuery(id+"F1.wireOp",EDGE,"E22.MirrorCS")])],"isStart":false}),makeQuery(id+"F5.opExtrude","SWEPT_EDGE",EDGE,{"disambiguationData":[OSD([sQuery(id+"F0.wireOp",EDGE,"E10.MirrorCS"),sQuery(id+"F0.wireOp",EDGE,"E12.MirrorCS"),sQuery(id+"F0.wireOp",EDGE,"E15")])]})]}),"instanceName":"2"});
            var Q31;
            Q31=makeQuery(id+"F8.opPattern","COPY",EDGE,{"derivedFrom":makeQuery(id+"F5.boolean.opBoolean","MERGE",EDGE,{"derivedFrom":[makeQuery(id+"F4.opExtrude","CAP_EDGE",EDGE,{"disambiguationData":[OSD([sQuery(id+"F1.wireOp",EDGE,"E22.MirrorCS")])],"isStart":false}),makeQuery(id+"F5.opExtrude","SWEPT_EDGE",EDGE,{"disambiguationData":[OSD([sQuery(id+"F0.wireOp",EDGE,"E10.MirrorCS"),sQuery(id+"F0.wireOp",EDGE,"E12.MirrorCS"),sQuery(id+"F0.wireOp",EDGE,"E15")])]})]}),"instanceName":"1"});
            var Q32;
            Q32=makeQuery(id+"F8.opPattern","COPY",EDGE,{"derivedFrom":makeQuery(id+"F5.boolean.opBoolean","MERGE",EDGE,{"derivedFrom":[makeQuery(id+"F4.opExtrude","CAP_EDGE",EDGE,{"disambiguationData":[OSD([sQuery(id+"F1.wireOp",EDGE,"E18")])],"isStart":false}),makeQuery(id+"F5.opExtrude","SWEPT_EDGE",EDGE,{"disambiguationData":[OSD([sQuery(id+"F0.wireOp",EDGE,"E10.MirrorCS"),sQuery(id+"F0.wireOp",EDGE,"E12.MirrorCS"),sQuery(id+"F0.wireOp",EDGE,"E15")])]})]}),"instanceName":"1"});
            var Q33;
            Q33=makeQuery(id+"F8.opPattern","COPY",EDGE,{"derivedFrom":makeQuery(id+"F4.opExtrude","CAP_EDGE",EDGE,{"disambiguationData":[OSD([sQuery(id+"F1.wireOp",EDGE,"E21.MirrorCS")])],"isStart":false}),"instanceName":"1"});
            var Q34;
            {var subQ0=sQuery(id+"F1.wireOp",EDGE,"E25");var subQ1=sQuery(id+"F1.wireOp",EDGE,"E19");var subQ2=sQuery(id+"F1.wireOp",EDGE,"E17");var subQ3=makeQuery(id+"F7.boolean.opBoolean","MERGE",EDGE,{"derivedFrom":[makeQuery(id+"F4.opExtrude","SWEPT_EDGE",EDGE,{"disambiguationData":[OSD([subQ2,subQ1,subQ0])]}),makeQuery(id+"F7.opExtrude","SWEPT_EDGE",EDGE,{"disambiguationData":[OSD([subQ2,subQ1,subQ0])]})]});Q34=makeQuery(id+"F8.boolean.opBoolean","MERGE",EDGE,{"derivedFrom":[subQ3,makeQuery(id+"F8.opPattern","COPY",EDGE,{"derivedFrom":subQ3,"instanceName":"1"})]});}
            var Q35;
            {var subQ0=sQuery(id+"F1.wireOp",EDGE,"E25");var subQ1=sQuery(id+"F1.wireOp",EDGE,"E16.1");var subQ2=sQuery(id+"F1.wireOp",EDGE,"E16.0");var subQ3=makeQuery(id+"F7.boolean.opBoolean","MERGE",EDGE,{"derivedFrom":[makeQuery(id+"F6.boolean.opBoolean","COPY",EDGE,{"derivedFrom":makeQuery(id+"F6.opExtrude","SWEPT_EDGE",EDGE,{"disambiguationData":[OSD([subQ2,subQ1,subQ0])]})}),makeQuery(id+"F7.opExtrude","SWEPT_EDGE",EDGE,{"disambiguationData":[OSD([subQ2,subQ1,subQ0])]})]});Q35=makeQuery(id+"F8.boolean.opBoolean","MERGE",EDGE,{"derivedFrom":[subQ3,makeQuery(id+"F8.opPattern","COPY",EDGE,{"derivedFrom":subQ3,"instanceName":"1"})]});}
            var Q36;
            {var subQ0=sQuery(id+"F1.wireOp",EDGE,"E24");var subQ1=sQuery(id+"F1.wireOp",EDGE,"E21.MirrorCS");var subQ2=sQuery(id+"F1.wireOp",EDGE,"E17");var subQ3=makeQuery(id+"F7.boolean.opBoolean","MERGE",EDGE,{"derivedFrom":[makeQuery(id+"F4.opExtrude","SWEPT_EDGE",EDGE,{"disambiguationData":[OSD([subQ2,subQ1,subQ0])]}),makeQuery(id+"F7.opExtrude","SWEPT_EDGE",EDGE,{"disambiguationData":[OSD([subQ2,subQ1,subQ0])]})]});Q36=makeQuery(id+"F8.boolean.opBoolean","MERGE",EDGE,{"derivedFrom":[subQ3,makeQuery(id+"F8.opPattern","COPY",EDGE,{"derivedFrom":subQ3,"instanceName":"1"})]});}
            var Q37;
            {var subQ0=sQuery(id+"F1.wireOp",EDGE,"E24");var subQ1=sQuery(id+"F1.wireOp",EDGE,"E16.4");var subQ2=sQuery(id+"F1.wireOp",EDGE,"E16.3");var subQ3=makeQuery(id+"F7.boolean.opBoolean","MERGE",EDGE,{"derivedFrom":[makeQuery(id+"F6.boolean.opBoolean","COPY",EDGE,{"derivedFrom":makeQuery(id+"F6.opExtrude","SWEPT_EDGE",EDGE,{"disambiguationData":[OSD([subQ2,subQ1,subQ0])]})}),makeQuery(id+"F7.opExtrude","SWEPT_EDGE",EDGE,{"disambiguationData":[OSD([subQ2,subQ1,subQ0])]})]});Q37=makeQuery(id+"F8.boolean.opBoolean","MERGE",EDGE,{"derivedFrom":[subQ3,makeQuery(id+"F8.opPattern","COPY",EDGE,{"derivedFrom":subQ3,"instanceName":"1"})]});}
            var Q38;
            Q38=makeQuery(id+"F4.opExtrude","CAP_EDGE",EDGE,{"disambiguationData":[OSD([sQuery(id+"F1.wireOp",EDGE,"E19")])],"isStart":false});
            var Q39;
            Q39=makeQuery(id+"F9.opPattern","COPY",EDGE,{"derivedFrom":makeQuery(id+"F4.opExtrude","CAP_EDGE",EDGE,{"disambiguationData":[OSD([sQuery(id+"F1.wireOp",EDGE,"E19")])],"isStart":false}),"instanceName":"2"});
            var Q40;
            Q40=makeQuery(id+"F8.opPattern","COPY",EDGE,{"derivedFrom":makeQuery(id+"F4.opExtrude","CAP_EDGE",EDGE,{"disambiguationData":[OSD([sQuery(id+"F1.wireOp",EDGE,"E19")])],"isStart":false}),"instanceName":"1"});
            var Q41;
            {var subQ0=makeQuery(id+"F5.opExtrude","CAP_EDGE",EDGE,{"disambiguationData":[OSD([sQuery(id+"F0.wireOp",EDGE,"E15")])],"isStart":true});Q41=makeQuery(id+"F9.boolean.opBoolean","MERGE",EDGE,{"derivedFrom":[makeQuery(id+"F8.opPattern","COPY",EDGE,{"derivedFrom":subQ0,"instanceName":"1"}),makeQuery(id+"F9.opPattern","COPY",EDGE,{"derivedFrom":subQ0,"instanceName":"2"})]});}
            var Q42;
            Q42=makeQuery(id+"F9.opPattern","COPY",EDGE,{"derivedFrom":makeQuery(id+"F8.opPattern","COPY",EDGE,{"derivedFrom":makeQuery(id+"F4.opExtrude","CAP_EDGE",EDGE,{"disambiguationData":[OSD([sQuery(id+"F1.wireOp",EDGE,"E21.MirrorCS")])],"isStart":false}),"instanceName":"1"}),"instanceName":"1"});
            var Q43;
            {var subQ0=sQuery(id+"F0.wireOp",EDGE,"E15");var subQ17=makeQuery(id+"F5.opExtrude","SWEPT_FACE",FACE,{"disambiguationData":[OSD([subQ0])]});Q43=makeQuery(id+"FdFZlNH1jCsqDf1_2.boolean.opBoolean","INTERSECT",EDGE,{"derivedFrom":[makeQuery(id+"F12.boolean.opBoolean","SPLIT",FACE,{"disambiguationData":[TD([makeQuery(id+"F9.opPattern","COPY",FACE,{"derivedFrom":makeQuery(id+"F3.opRevolve","SWEPT_FACE",FACE,{"disambiguationData":[OSD([sQuery(id+"F0.wireOp",EDGE,"E2")])]}),"instanceName":"1"})])],"derivedFrom":makeQuery(id+"F9.boolean.opBoolean","MERGE",FACE,{"derivedFrom":[makeQuery(id+"F9.opPattern","COPY",FACE,{"derivedFrom":subQ17,"instanceName":"1"}),makeQuery(id+"F9.opPattern","COPY",FACE,{"derivedFrom":makeQuery(id+"F8.opPattern","COPY",FACE,{"derivedFrom":subQ17,"instanceName":"1"}),"instanceName":"2"})]})}),makeQuery(id+"FdFZlNH1jCsqDf1_2.opExtrude","SWEPT_FACE",FACE,{"disambiguationData":[OSD([sQuery(id+"F11.wireOp",EDGE,"E54")])]})]});}
            var Q44;
            {var subQ2=sQuery(id+"F0.wireOp",EDGE,"E15");var subQ17=makeQuery(id+"F5.opExtrude","SWEPT_FACE",FACE,{"disambiguationData":[OSD([subQ2])]});Q44=makeQuery(id+"FdFZlNH1jCsqDf1_2.boolean.opBoolean","INTERSECT",EDGE,{"derivedFrom":[makeQuery(id+"F12.boolean.opBoolean","SPLIT",FACE,{"disambiguationData":[TD([makeQuery(id+"F9.opPattern","COPY",FACE,{"derivedFrom":makeQuery(id+"F8.opPattern","COPY",FACE,{"derivedFrom":makeQuery(id+"F3.opRevolve","SWEPT_FACE",FACE,{"disambiguationData":[OSD([sQuery(id+"F0.wireOp",EDGE,"E2")])]}),"instanceName":"1"}),"instanceName":"2"})])],"derivedFrom":makeQuery(id+"F9.boolean.opBoolean","MERGE",FACE,{"derivedFrom":[makeQuery(id+"F9.opPattern","COPY",FACE,{"derivedFrom":subQ17,"instanceName":"1"}),makeQuery(id+"F9.opPattern","COPY",FACE,{"derivedFrom":makeQuery(id+"F8.opPattern","COPY",FACE,{"derivedFrom":subQ17,"instanceName":"1"}),"instanceName":"2"})]})}),makeQuery(id+"FdFZlNH1jCsqDf1_2.opExtrude","SWEPT_FACE",FACE,{"disambiguationData":[OSD([sQuery(id+"F11.wireOp",EDGE,"E54")])]})]});}
            var Q45;
            Q45=makeQuery(id+"F10.boolean.opBoolean","COPY",EDGE,{"derivedFrom":makeQuery(id+"F10.opExtrude","CAP_EDGE",EDGE,{"disambiguationData":[OSD([sQuery(id+"F2.wireOp",EDGE,"E36.MirrorCS")])],"isStart":true})});
            var Q46;
            Q46=makeQuery(id+"F10.boolean.opBoolean","COPY",EDGE,{"derivedFrom":makeQuery(id+"F10.opExtrude","CAP_EDGE",EDGE,{"disambiguationData":[OSD([sQuery(id+"F2.wireOp",EDGE,"E37.MirrorCS"),sQuery(id+"F2.wireOp",EDGE,"E47.MirrorCS")])],"isStart":true})});
            var Q47;
            Q47=makeQuery(id+"F10.boolean.opBoolean","COPY",EDGE,{"derivedFrom":makeQuery(id+"F10.opExtrude","CAP_EDGE",EDGE,{"disambiguationData":[OSD([sQuery(id+"F2.wireOp",EDGE,"E35.MirrorCS")])],"isStart":true})});
            var Q48;
            Q48=makeQuery(id+"F10.boolean.opBoolean","COPY",EDGE,{"derivedFrom":makeQuery(id+"F10.opExtrude","CAP_EDGE",EDGE,{"disambiguationData":[OSD([sQuery(id+"F2.wireOp",EDGE,"E34")])],"isStart":true})});
            var Q49;
            Q49=makeQuery(id+"F10.boolean.opBoolean","COPY",EDGE,{"derivedFrom":makeQuery(id+"F10.opExtrude","CAP_EDGE",EDGE,{"disambiguationData":[OSD([sQuery(id+"F2.wireOp",EDGE,"E39.filletArc")])],"isStart":true})});
            var Q50;
            Q50=makeQuery(id+"F10.boolean.opBoolean","COPY",EDGE,{"derivedFrom":makeQuery(id+"F10.opExtrude","CAP_EDGE",EDGE,{"disambiguationData":[OSD([sQuery(id+"F2.wireOp",EDGE,"E32")])],"isStart":true})});
            var Q51;
            Q51=makeQuery(id+"F10.boolean.opBoolean","COPY",EDGE,{"derivedFrom":makeQuery(id+"F10.opExtrude","CAP_EDGE",EDGE,{"disambiguationData":[OSD([sQuery(id+"F2.wireOp",EDGE,"E33"),sQuery(id+"F2.wireOp",EDGE,"E42.MirrorCS")])],"isStart":true})});
            var Q52;
            Q52=makeQuery(id+"F10.boolean.opBoolean","COPY",EDGE,{"derivedFrom":makeQuery(id+"F10.opExtrude","CAP_EDGE",EDGE,{"disambiguationData":[OSD([sQuery(id+"F2.wireOp",EDGE,"E43.MirrorCS")])],"isStart":true})});
            var Q53;
            Q53=makeQuery(id+"F10.boolean.opBoolean","COPY",EDGE,{"derivedFrom":makeQuery(id+"F10.opExtrude","CAP_EDGE",EDGE,{"disambiguationData":[OSD([sQuery(id+"F2.wireOp",EDGE,"E44.MirrorCS")])],"isStart":true})});
            var Q54;
            Q54=makeQuery(id+"F10.boolean.opBoolean","COPY",EDGE,{"derivedFrom":makeQuery(id+"F10.opExtrude","CAP_EDGE",EDGE,{"disambiguationData":[OSD([sQuery(id+"F2.wireOp",EDGE,"E45.MirrorCS")])],"isStart":true})});
            var Q55;
            Q55=makeQuery(id+"F10.boolean.opBoolean","COPY",EDGE,{"derivedFrom":makeQuery(id+"F10.opExtrude","CAP_EDGE",EDGE,{"disambiguationData":[OSD([sQuery(id+"F2.wireOp",EDGE,"E46.MirrorCS")])],"isStart":true})});
            var Q56;
            Q56=makeQuery(id+"F10.boolean.opBoolean","COPY",EDGE,{"derivedFrom":makeQuery(id+"F10.opExtrude","CAP_EDGE",EDGE,{"disambiguationData":[OSD([sQuery(id+"F2.wireOp",EDGE,"E48.MirrorCS")])],"isStart":true})});
            var Q57;
            Q57=makeQuery(id+"F10.boolean.opBoolean","COPY",EDGE,{"derivedFrom":makeQuery(id+"F10.opExtrude","CAP_EDGE",EDGE,{"disambiguationData":[OSD([sQuery(id+"F2.wireOp",EDGE,"E46.MirrorCS")])],"isStart":false})});
            var Q58;
            Q58=makeQuery(id+"F10.boolean.opBoolean","COPY",EDGE,{"derivedFrom":makeQuery(id+"F10.opExtrude","CAP_EDGE",EDGE,{"disambiguationData":[OSD([sQuery(id+"F2.wireOp",EDGE,"E45.MirrorCS")])],"isStart":false})});
            var Q59;
            Q59=makeQuery(id+"F10.boolean.opBoolean","COPY",EDGE,{"derivedFrom":makeQuery(id+"F10.opExtrude","CAP_EDGE",EDGE,{"disambiguationData":[OSD([sQuery(id+"F2.wireOp",EDGE,"E44.MirrorCS")])],"isStart":false})});
            var Q60;
            Q60=makeQuery(id+"F10.boolean.opBoolean","COPY",EDGE,{"derivedFrom":makeQuery(id+"F10.opExtrude","CAP_EDGE",EDGE,{"disambiguationData":[OSD([sQuery(id+"F2.wireOp",EDGE,"E43.MirrorCS")])],"isStart":false})});
            var Q61;
            Q61=makeQuery(id+"F10.boolean.opBoolean","COPY",EDGE,{"derivedFrom":makeQuery(id+"F10.opExtrude","CAP_EDGE",EDGE,{"disambiguationData":[OSD([sQuery(id+"F2.wireOp",EDGE,"E33"),sQuery(id+"F2.wireOp",EDGE,"E42.MirrorCS")])],"isStart":false})});
            var Q62;
            Q62=makeQuery(id+"F10.boolean.opBoolean","COPY",EDGE,{"derivedFrom":makeQuery(id+"F10.opExtrude","CAP_EDGE",EDGE,{"disambiguationData":[OSD([sQuery(id+"F2.wireOp",EDGE,"E32")])],"isStart":false})});
            var Q63;
            Q63=makeQuery(id+"F10.boolean.opBoolean","COPY",EDGE,{"derivedFrom":makeQuery(id+"F10.opExtrude","CAP_EDGE",EDGE,{"disambiguationData":[OSD([sQuery(id+"F2.wireOp",EDGE,"E34")])],"isStart":false})});
            var Q64;
            Q64=makeQuery(id+"F10.boolean.opBoolean","COPY",EDGE,{"derivedFrom":makeQuery(id+"F10.opExtrude","CAP_EDGE",EDGE,{"disambiguationData":[OSD([sQuery(id+"F2.wireOp",EDGE,"E39.filletArc")])],"isStart":false})});
            var Q65;
            Q65=makeQuery(id+"F10.boolean.opBoolean","COPY",EDGE,{"derivedFrom":makeQuery(id+"F10.opExtrude","CAP_EDGE",EDGE,{"disambiguationData":[OSD([sQuery(id+"F2.wireOp",EDGE,"E35.MirrorCS")])],"isStart":false})});
            var Q66;
            Q66=makeQuery(id+"F10.boolean.opBoolean","COPY",EDGE,{"derivedFrom":makeQuery(id+"F10.opExtrude","CAP_EDGE",EDGE,{"disambiguationData":[OSD([sQuery(id+"F2.wireOp",EDGE,"E36.MirrorCS")])],"isStart":false})});
            var Q67;
            Q67=makeQuery(id+"F10.boolean.opBoolean","COPY",EDGE,{"derivedFrom":makeQuery(id+"F10.opExtrude","CAP_EDGE",EDGE,{"disambiguationData":[OSD([sQuery(id+"F2.wireOp",EDGE,"E37.MirrorCS"),sQuery(id+"F2.wireOp",EDGE,"E47.MirrorCS")])],"isStart":false})});
            var Q68;
            Q68=makeQuery(id+"F10.boolean.opBoolean","COPY",EDGE,{"derivedFrom":makeQuery(id+"F10.opExtrude","CAP_EDGE",EDGE,{"disambiguationData":[OSD([sQuery(id+"F2.wireOp",EDGE,"E48.MirrorCS")])],"isStart":false})});
            var Q69;
            Q69=makeQuery(id+"F10.boolean.opBoolean","COPY",EDGE,{"derivedFrom":makeQuery(id+"F10.opExtrude","CAP_EDGE",EDGE,{"disambiguationData":[OSD([sQuery(id+"F2.wireOp",EDGE,"E51.MirrorC")])],"isStart":true})});
            var Q70;
            Q70=makeQuery(id+"F10.boolean.opBoolean","COPY",EDGE,{"derivedFrom":makeQuery(id+"F10.opExtrude","CAP_EDGE",EDGE,{"disambiguationData":[OSD([sQuery(id+"F2.wireOp",EDGE,"E51.MirrorC")])],"isStart":false})});
            var Q71;
            Q71=makeQuery(id+"F10.boolean.opBoolean","COPY",EDGE,{"derivedFrom":makeQuery(id+"F10.opExtrude","CAP_EDGE",EDGE,{"disambiguationData":[OSD([sQuery(id+"F2.wireOp",EDGE,"E50")])],"isStart":false})});
            var Q72;
            Q72=makeQuery(id+"F10.boolean.opBoolean","COPY",EDGE,{"derivedFrom":makeQuery(id+"F10.opExtrude","CAP_EDGE",EDGE,{"disambiguationData":[OSD([sQuery(id+"F2.wireOp",EDGE,"E50")])],"isStart":true})});
            fillet(context, id + "F14", {"entities" : qUnion([Q0, Q1, Q2, Q3, Q4, Q5, Q6, Q7, Q8, Q9, Q10, Q11, Q12, Q13, Q14, Q15, Q16, Q17, Q18, Q19, Q20, Q21, Q22, Q23, Q24, Q25, Q26, Q27, Q28, Q29, Q30, Q31, Q32, Q33, Q34, Q35, Q36, Q37, Q38, Q39, Q40, Q41, Q42, Q43, Q44, Q45, Q46, Q47, Q48, Q49, Q50, Q51, Q52, Q53, Q54, Q55, Q56, Q57, Q58, Q59, Q60, Q61, Q62, Q63, Q64, Q65, Q66, Q67, Q68, Q69, Q70, Q71, Q72]), "radius" : .5 * mm, "tangentPropagation" : true, "allowEdgeOverflow" : false});
        }
    });
